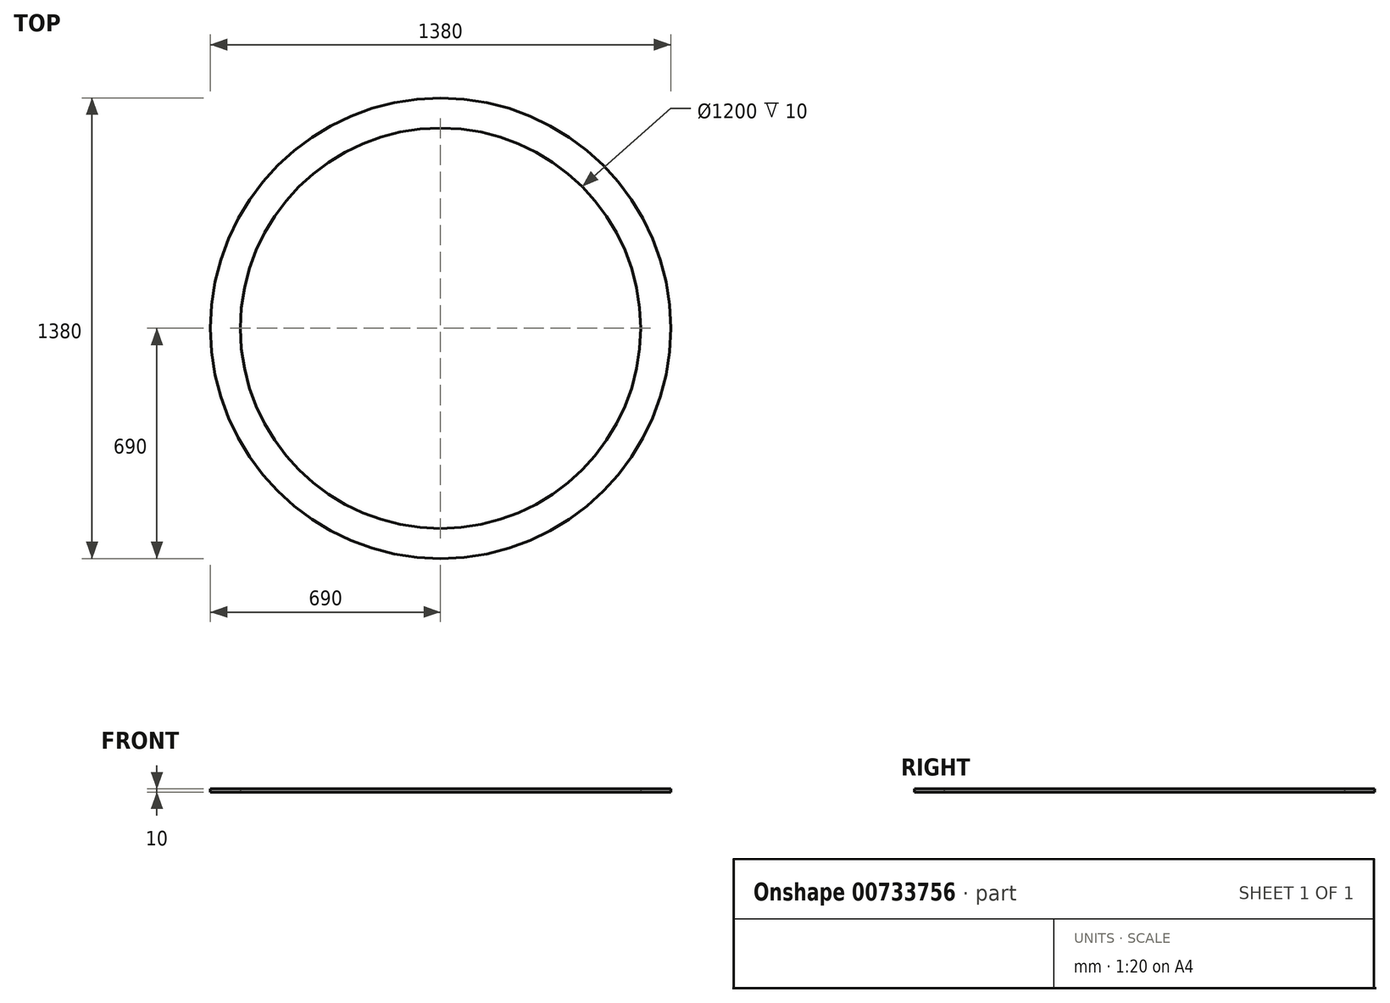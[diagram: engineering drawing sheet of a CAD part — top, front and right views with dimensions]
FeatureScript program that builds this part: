
annotation { "Feature Type Name" : "Feature", "Feature Type Description" : "" }
export const myFeature = defineFeature(function(context is Context, id is Id, definition is map)
    precondition{}
    {
        {
            var Q0;
            Q0=qCreatedBy(makeId("Top.planeOp"),FACE);
            var sketch = newSketch(context, id + "F0", { "sketchPlane" : qUnion([Q0])});
            skCircle(sketch, "E0", {"center": v(0, 0) * mm, "radius": 600 * mm});
            skCircle(sketch, "E1", {"center": v(0, 0) * mm, "radius": 690 * mm});
            skSolve(sketch);
        }
        {
            var Q0;
            Q0=makeQuery(id+"F0.imprint","IMPRINT",FACE,{"disambiguationData":[TD([[makeQuery(id+"F0.imprint","IMPRINT",EDGE,{"derivedFrom":sQuery(id+"F0.wireOp",EDGE,"E0")}),-1.0]])]});
            extrude(context, id + "F1", {"entities" : qUnion([Q0]), "depth" : 10 * mm, "offsetDistance" : 25 * mm});
        }
    });
